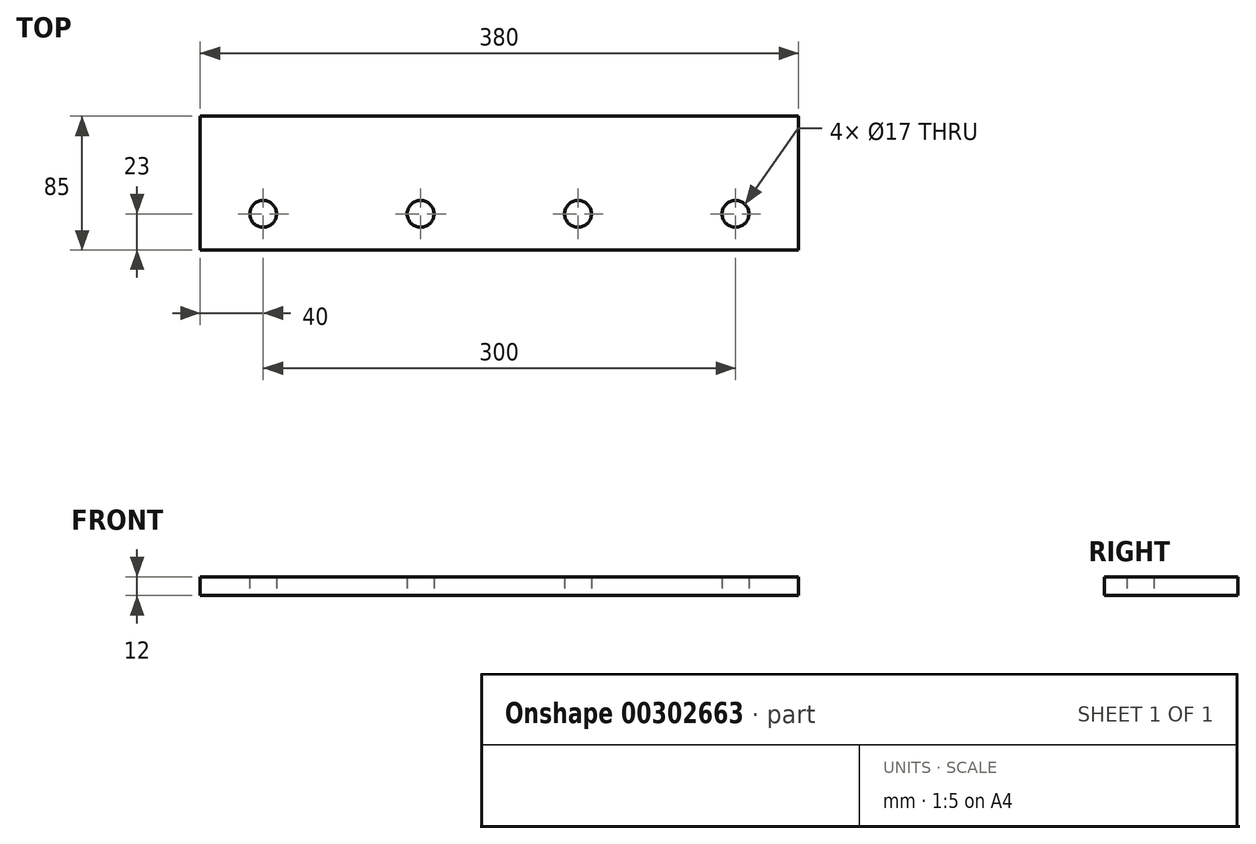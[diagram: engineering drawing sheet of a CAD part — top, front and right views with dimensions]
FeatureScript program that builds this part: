
annotation { "Feature Type Name" : "Feature", "Feature Type Description" : "" }
export const myFeature = defineFeature(function(context is Context, id is Id, definition is map)
    precondition{}
    {
        {
            var Q0;
            Q0=qCreatedBy(makeId("Top.planeOp"),FACE);
            var sketch = newSketch(context, id + "F0", { "sketchPlane" : qUnion([Q0])});
            skLineSegment(sketch, "E0.bottom", {"start": v(0, 0) * mm, "end": v(380, 0) * mm});
            skLineSegment(sketch, "E0.top", {"start": v(0, 85) * mm, "end": v(380, 85) * mm});
            skLineSegment(sketch, "E0.left", {"start": v(0, 0) * mm, "end": v(0, 85) * mm});
            skLineSegment(sketch, "E0.right", {"start": v(380, 0) * mm, "end": v(380, 85) * mm});
            skLineSegment(sketch, "E1", {"start": v(190, 125.6) * mm, "end": v(190, -230.75) * mm});
            skCircle(sketch, "E2", {"center": v(240, 23) * mm, "radius": 8.5 * mm});
            skCircle(sketch, "E3", {"center": v(340, 23) * mm, "radius": 8.5 * mm});
            skCircle(sketch, "E4.MirrorC", {"center": v(140, 23) * mm, "radius": 8.5 * mm});
            skCircle(sketch, "E5.MirrorC", {"center": v(40, 23) * mm, "radius": 8.5 * mm});
            skSolve(sketch);
        }
        {
            var Q0;
            Q0=qSketchRegion(id+"F0",true);
            extrude(context, id + "F1", {"entities" : qUnion([Q0]), "depth" : 12 * mm});
        }
    });
